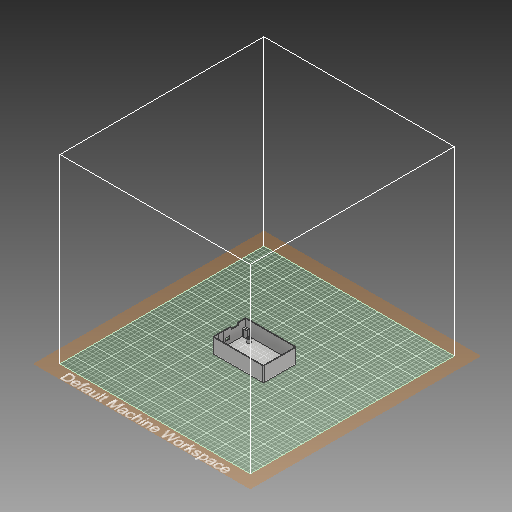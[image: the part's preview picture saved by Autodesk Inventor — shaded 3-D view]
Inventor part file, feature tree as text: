
AUTODESK INVENTOR PART (.ipt)
format: ipt  version: 2019 (Build 230136000, 136)  size: 451,584 bytes
history: native  units: mm
features: other x9, extrude x7, hole x2, fillet x1
ambient origin geometry x8: Origin, YZ Plane, XZ Plane, XY Plane, X Axis, Y Axis, Z Axis, Center Point
bodies: Solid1 (feature_tree)
feature tree (19):
  extrude  "Extrusion1"  Depth=109.0mm
  extrude  "Extrusion2"  Depth=70.0mm
  other  "stena_RJ45"
  other  "srouby_upevneni"
  extrude  "Extrusion3"  Depth=1.2mm TaperAngle=0.0deg
  extrude  "Extrusion4"  Depth=8.0mm
  extrude  "Extrusion5"  Depth=17.0mm
  hole  "Hole1"  [1 undecoded]
  hole  "Hole2"  [1 undecoded]
  extrude  "Extrusion7"  Depth=74.9mm
  extrude  "Extrusion8"  Depth=8.0mm
  fillet  "Fillet1"  Radius=82.0mm
  other  "zaklad"
  other  "uchyt_pro_desku"
  other  "steny"
  other  "diry"
  other  "uchyt_pro_desku_diry"
  other  "dira_USB"
  other  "vyrez_napajeci_jack_nepouzivany"
note: 2 required parameter values undecoded (feature->parameter linkage not recoverable at this tier; creation-order binding heuristic only, values carry confidence <= 0.55)
